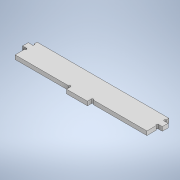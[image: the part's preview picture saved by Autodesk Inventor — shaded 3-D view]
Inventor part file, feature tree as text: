
AUTODESK INVENTOR PART (.ipt)
format: ipt  version: 2020 (Build 240168000, 168)  size: 137,728 bytes
history: native  units: mm
features: extrude x1, sketch x1
ambient origin geometry x8: Origin, YZ Plane, XZ Plane, XY Plane, X Axis, Y Axis, Z Axis, Center Point
bodies: Solid1 (feature_tree)
feature tree (2):
  extrude  "Extrusion1"  Depth=97.083333mm
  sketch  "Sketch1"  dims[d2=3.5mm d5=3.5mm d9=7.0mm d11=10.0mm d24=7.0mm d25=0.0mm d27=36.5mm d32=5.0mm d33=230.666667mm d36=7.0mm d41=3.5mm d42=3.5mm d43=97.083333mm]
